# Revit family: FP-Revit20-en-RS3684WLUVE1-IntegratedRefrigerator-0-90003566A-US-CA
name_source: partatom
category: Specialty Equipment
units: mm (PartAtom-declared; Revit-internal decimal feet)

## family parameters
Always vertical = Yes
Cut with Voids When Loaded = Yes
OmniClass Number = 23.40.40.11.11
OmniClass Title = Refrigerators and Freezers
Part Type = Normal
Room Calculation Point = No
Round Connector Dimension = Use Diameter
Shared = No
Work Plane-Based = No

## types (1)
- RS3684WRUVE1
    Cavity - Depth = 635 mm
    Cavity - Height = 2134 mm  [stored 7.00131 ft]
    Cavity - Width = 914 mm  [stored 2.99869 ft]
    Connector Description - Electrical = 120 V, 10 amp fused electrical supply
    Default Elevation = 0 mm  [stored 0 ft]
    Description = 30" Integrated Column Freezer with internal Ice & Water, White Interior
    Handle Style - Contemporary Round (AHSRD3684W) = No
    Handle Style - Contemporary Square (AHD3RD3684W) = No
    Handle Style - Contemporary Square Fine (AHD5RD3684W) = No
    Handle Style - Contemporary Square Fine Black (AHD5RD3684WB) = No
    Handle Style - Professional Round  (AHCRD3684W) = Yes
    Handle Style - Professional Round Brass (AHCRD3684WBA) = No
    Handle Style - Professional Round Dark Copper (AHCRD3684WDC) = No
    Left Hinging Options = Hinge conversion and left hand stainless steel panels (RD3684WLD) are available
    Manufacturer = Fisher & Paykel Appliances
    Material - Body = Fisher & Paykel - Grey
    Material - Door Front = Fisher & Paykel - Stainless Steel
    Material - Door Structure = Fisher & Paykel - Stainless Steel
    Material - Handle = Fisher & Paykel - Aluminium
    Model = RS3084WLU1
    Product - Depth (exl front panel) = 610 mm  [stored 2.00131 ft]
    Product - Height = 2134 mm  [stored 7.00131 ft]
    Product - Width = 908 mm  [stored 2.979 ft]
    Stainless Steel Door Panels (RD3684WLD) = No
    URL = www.fisherpaykel.com
    Visibility - Clearance Required = Yes
    Visibility - Visibility Control Note = Yes
    Visibility - Water Connection = Yes

note: [stored X ft] marks values corroborated as IEEE doubles in the binary element streams (Revit-internal decimal feet)

## geometry (parser evidence)
native form markers: Sweep x26
no freeform markers — native parametric forms only
